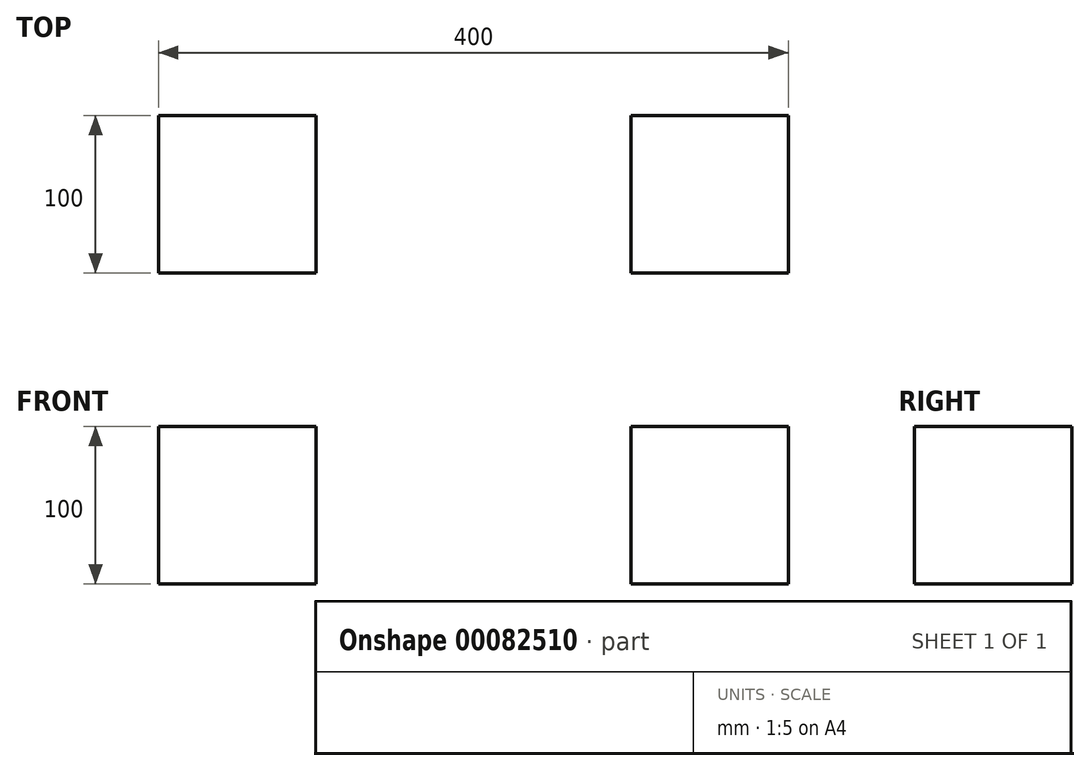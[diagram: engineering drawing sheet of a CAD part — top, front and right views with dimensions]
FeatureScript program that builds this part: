
annotation { "Feature Type Name" : "Feature", "Feature Type Description" : "" }
export const myFeature = defineFeature(function(context is Context, id is Id, definition is map)
    precondition{}
    {
        {
            var Q0;
            Q0=qCreatedBy(makeId("Front.planeOp"),FACE);
            var sketch = newSketch(context, id + "F0", { "sketchPlane" : qUnion([Q0])});
            skLineSegment(sketch, "E0.bottom", {"start": v(0, 0) * mm, "end": v(100, 0) * mm});
            skLineSegment(sketch, "E0.top", {"start": v(0, 100) * mm, "end": v(100, 100) * mm});
            skLineSegment(sketch, "E0.left", {"start": v(0, 0) * mm, "end": v(0, 100) * mm});
            skLineSegment(sketch, "E0.right", {"start": v(100, 0) * mm, "end": v(100, 100) * mm});
            skSolve(sketch);
        }
        {
            var Q0;
            Q0=qSketchRegion(id+"F0",true);
            extrude(context, id + "F1", {"entities" : qUnion([Q0]), "depth" : 100 * mm});
        }
        {
            var Q0;
            Q0=makeQuery(id+"F1.opExtrude","SWEPT_BODY",BODY,{"disambiguationData":[OSD([sQuery(id+"F0.wireOp",EDGE,"E0.bottom"),sQuery(id+"F0.wireOp",EDGE,"E0.top"),sQuery(id+"F0.wireOp",EDGE,"E0.left"),sQuery(id+"F0.wireOp",EDGE,"E0.right")])]});
            transform(context, id + "F2", {"entities" : qUnion([Q0]), "transformType" : TransformType.TRANSLATION_3D, "dx" : 300 * mm, "dy" : 0 * mm, "dz" : 0 * mm, "makeCopy" : true});
        }
    });
